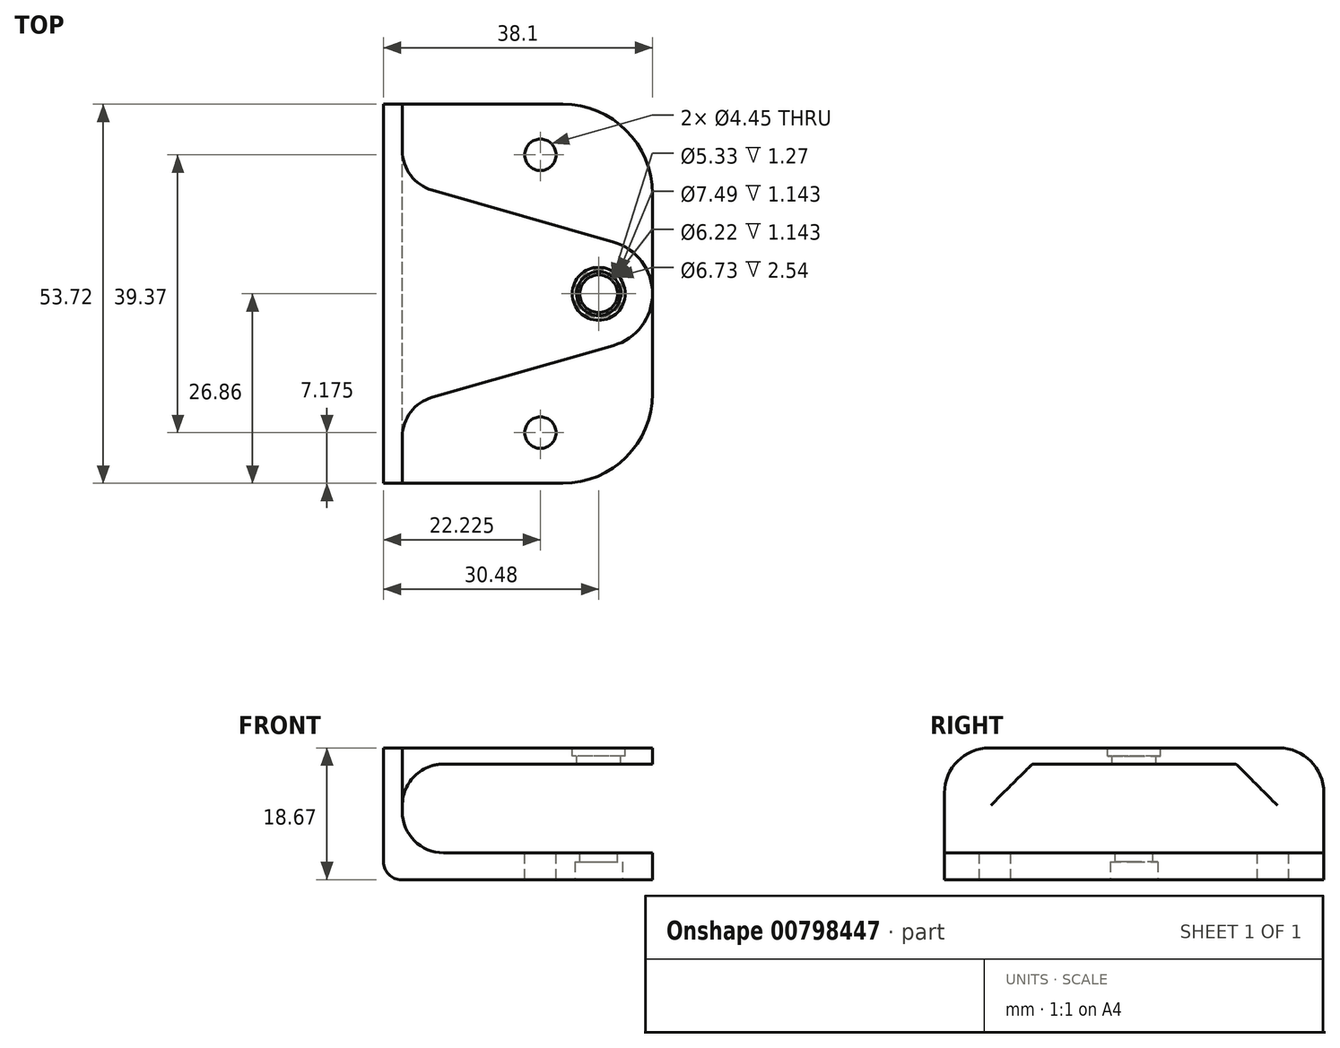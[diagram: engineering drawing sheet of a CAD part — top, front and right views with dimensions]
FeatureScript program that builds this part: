
annotation { "Feature Type Name" : "Feature", "Feature Type Description" : "" }
export const myFeature = defineFeature(function(context is Context, id is Id, definition is map)
    precondition{}
    {
        {
            var Q0;
            Q0=qCreatedBy(makeId("Front.planeOp"),FACE);
            var sketch = newSketch(context, id + "F0", { "sketchPlane" : qUnion([Q0])});
            skLineSegment(sketch, "E0", {"start": v(38.1, 0) * mm, "end": v(0, 0) * mm});
            skLineSegment(sketch, "E1", {"start": v(0, 0) * mm, "end": v(0, 18.67) * mm});
            skLineSegment(sketch, "E2", {"start": v(0, 18.67) * mm, "end": v(38.1, 18.67) * mm});
            skLineSegment(sketch, "E3", {"start": v(38.1, 18.67) * mm, "end": v(38.1, 16.38) * mm});
            skLineSegment(sketch, "E4", {"start": v(38.1, 16.38) * mm, "end": v(2.67, 16.38) * mm});
            skLineSegment(sketch, "E5", {"start": v(2.67, 16.38) * mm, "end": v(2.67, 3.8) * mm});
            skLineSegment(sketch, "E6", {"start": v(2.67, 3.8) * mm, "end": v(38.1, 3.81) * mm});
            skLineSegment(sketch, "E7", {"start": v(38.1, 3.81) * mm, "end": v(38.1, 0) * mm});
            skSolve(sketch);
        }
        {
            var Q0;
            Q0=makeQuery(id+"F0.imprint","IMPRINT",FACE,{"disambiguationData":[TD([[makeQuery(id+"F0.imprint","IMPRINT",EDGE,{"derivedFrom":sQuery(id+"F0.wireOp",EDGE,"E0")}),-1.0]])]});
            extrude(context, id + "F1", {"entities" : qUnion([Q0]), "endBound" : BoundingType.SYMMETRIC, "depth" : 53.72 * mm, "offsetDistance" : 25.4 * mm});
        }
        {
            var Q0;
            Q0=makeQuery(id+"F1.opExtrude","SWEPT_FACE",FACE,{"disambiguationData":[OSD([sQuery(id+"F0.wireOp",EDGE,"E6")])]});
            var sketch = newSketch(context, id + "F2", { "sketchPlane" : qUnion([Q0])});
            skCircle(sketch, "E8", {"center": v(22.23, 19.69) * mm, "radius": 2.22 * mm});
            skCircle(sketch, "E9", {"center": v(22.23, -19.69) * mm, "radius": 2.22 * mm});
            skCircle(sketch, "E10", {"center": v(30.48, 0) * mm, "radius": 2.67 * mm});
            skSolve(sketch);
        }
        {
            var Q0;
            Q0=makeQuery(id+"F2.imprint","IMPRINT",FACE,{"disambiguationData":[TD([[makeQuery(id+"F2.imprint","IMPRINT",EDGE,{"derivedFrom":sQuery(id+"F2.wireOp",EDGE,"E10")}),1.0]])]});
            var Q1;
            Q1=makeQuery(id+"F2.imprint","IMPRINT",FACE,{"disambiguationData":[TD([[makeQuery(id+"F2.imprint","IMPRINT",EDGE,{"derivedFrom":sQuery(id+"F2.wireOp",EDGE,"E8")}),1.0]])]});
            var Q2;
            Q2=makeQuery(id+"F2.imprint","IMPRINT",FACE,{"disambiguationData":[TD([[makeQuery(id+"F2.imprint","IMPRINT",EDGE,{"derivedFrom":sQuery(id+"F2.wireOp",EDGE,"E9")}),1.0]])]});
            extrude(context, id + "F3", {"entities" : qUnion([Q0, Q1, Q2]), "operationType" : NewBodyOperationType.REMOVE, "endBound" : BoundingType.THROUGH_ALL, "oppositeDirection" : true, "depth" : 25.4 * mm, "offsetDistance" : 25.4 * mm, "hasSecondDirection" : true, "secondDirectionBound" : SecondDirectionBoundingType.THROUGH_ALL, "secondDirectionOppositeDirection" : false, "secondDirectionDepth" : 25.4 * mm});
        }
        {
            var Q0;
            Q0=makeQuery(id+"F1.opExtrude","SWEPT_FACE",FACE,{"disambiguationData":[OSD([sQuery(id+"F0.wireOp",EDGE,"E2")])]});
            var sketch = newSketch(context, id + "F4", { "sketchPlane" : qUnion([Q0])});
            skLineSegment(sketch, "E11.0", {"start": v(2.67, -26.86) * mm, "end": v(2.67, 26.86) * mm, "construction": true});
            skCircle(sketch, "E12", {"center": v(30.48, 0) * mm, "radius": 7.62 * mm});
            skLineSegment(sketch, "E13", {"start": v(2.67, 15.87) * mm, "end": v(32.57, 7.33) * mm});
            skLineSegment(sketch, "E14", {"start": v(32.57, 7.33) * mm, "end": v(32.57, -7.33) * mm, "construction": true});
            skLineSegment(sketch, "E15", {"start": v(32.57, -7.33) * mm, "end": v(2.67, -15.88) * mm});
            skLineSegment(sketch, "E16", {"start": v(2.67, 15.87) * mm, "end": v(2.67, 26.86) * mm});
            skLineSegment(sketch, "E17", {"start": v(2.67, -15.88) * mm, "end": v(2.67, -26.86) * mm});
            skSolve(sketch);
        }
        {
            var Q0;
            {var subQ1=sQuery(id+"F4.wireOp",EDGE,"E13");Q0=makeQuery(id+"F4.imprint","IMPRINT",FACE,{"disambiguationData":[TD([[makeQuery(id+"F4.imprint","IMPRINT",EDGE,{"derivedFrom":subQ1}),1.0]])]});}
            var Q1;
            {var subQ2=sQuery(id+"F4.wireOp",EDGE,"E15");Q1=makeQuery(id+"F4.imprint","IMPRINT",FACE,{"disambiguationData":[TD([[makeQuery(id+"F4.imprint","IMPRINT",EDGE,{"derivedFrom":subQ2}),1.0]])]});}
            extrude(context, id + "F5", {"entities" : qUnion([Q0, Q1]), "operationType" : NewBodyOperationType.REMOVE, "endBound" : BoundingType.UP_TO_NEXT, "oppositeDirection" : true, "depth" : 25.4 * mm, "offsetDistance" : 25.4 * mm});
        }
        {
            var Q0;
            Q0=makeQuery(id+"F1.opExtrude","SWEPT_FACE",FACE,{"disambiguationData":[OSD([sQuery(id+"F0.wireOp",EDGE,"E2")])]});
            var sketch = newSketch(context, id + "F6", { "sketchPlane" : qUnion([Q0])});
            skCircle(sketch, "E18", {"center": v(30.48, 0) * mm, "radius": 3.75 * mm});
            skSolve(sketch);
        }
        {
            var Q0;
            Q0=makeQuery(id+"F6.imprint","IMPRINT",FACE,{"disambiguationData":[TD([[makeQuery(id+"F6.imprint","IMPRINT",EDGE,{"derivedFrom":sQuery(id+"F6.wireOp",EDGE,"E18")}),1.0]])]});
            extrude(context, id + "F7", {"entities" : qUnion([Q0]), "operationType" : NewBodyOperationType.REMOVE, "oppositeDirection" : true, "depth" : 1.14 * mm, "offsetDistance" : 25.4 * mm});
        }
        {
            var Q0;
            Q0=makeQuery(id+"F1.opExtrude","SWEPT_EDGE",EDGE,{"disambiguationData":[OSD([sQuery(id+"F0.wireOp",EDGE,"E5"),sQuery(id+"F0.wireOp",EDGE,"E6")])]});
            var Q1;
            Q1=makeQuery(id+"F1.opExtrude","SWEPT_EDGE",EDGE,{"disambiguationData":[OSD([sQuery(id+"F0.wireOp",EDGE,"E4"),sQuery(id+"F0.wireOp",EDGE,"E5")])]});
            var Q2;
            Q2=makeQuery(id+"F5.boolean.opBoolean","COPY",EDGE,{"derivedFrom":makeQuery(id+"F5.opExtrude","SWEPT_EDGE",EDGE,{"disambiguationData":[OSD([sQuery(id+"F4.wireOp",EDGE,"E13"),sQuery(id+"F4.wireOp",EDGE,"E16")])]})});
            var Q3;
            Q3=makeQuery(id+"F5.boolean.opBoolean","COPY",EDGE,{"derivedFrom":makeQuery(id+"F5.opExtrude","SWEPT_EDGE",EDGE,{"disambiguationData":[OSD([sQuery(id+"F4.wireOp",EDGE,"E15"),sQuery(id+"F4.wireOp",EDGE,"E17")])]})});
            fillet(context, id + "F8", {"entities" : qUnion([Q0, Q1, Q2, Q3]), "radius" : 5.84 * mm, "tangentPropagation" : true, "allowEdgeOverflow" : false});
        }
        {
            var Q0;
            Q0=makeQuery(id+"F1.opExtrude","CAP_EDGE",EDGE,{"disambiguationData":[OSD([sQuery(id+"F0.wireOp",EDGE,"E2")])],"isStart":true});
            var Q1;
            Q1=makeQuery(id+"F1.opExtrude","CAP_EDGE",EDGE,{"disambiguationData":[OSD([sQuery(id+"F0.wireOp",EDGE,"E2")])],"isStart":false});
            fillet(context, id + "F9", {"entities" : qUnion([Q0, Q1]), "radius" : 6.35 * mm, "tangentPropagation" : true, "allowEdgeOverflow" : false});
        }
        {
            var Q0;
            Q0=makeQuery(id+"F1.opExtrude","CAP_EDGE",EDGE,{"disambiguationData":[OSD([sQuery(id+"F0.wireOp",EDGE,"E7")])],"isStart":true});
            var Q1;
            Q1=makeQuery(id+"F1.opExtrude","CAP_EDGE",EDGE,{"disambiguationData":[OSD([sQuery(id+"F0.wireOp",EDGE,"E7")])],"isStart":false});
            fillet(context, id + "F10", {"entities" : qUnion([Q0, Q1]), "radius" : 12.7 * mm, "tangentPropagation" : true, "allowEdgeOverflow" : false});
        }
        {
            var Q0;
            Q0=makeQuery(id+"F1.opExtrude","SWEPT_EDGE",EDGE,{"disambiguationData":[OSD([sQuery(id+"F0.wireOp",EDGE,"E0"),sQuery(id+"F0.wireOp",EDGE,"E1")])]});
            fillet(context, id + "F11", {"entities" : qUnion([Q0]), "radius" : 2.54 * mm, "tangentPropagation" : true, "allowEdgeOverflow" : false});
        }
        {
            var Q0;
            Q0=makeQuery(id+"F7.boolean.opBoolean","COPY",FACE,{"derivedFrom":makeQuery(id+"F7.opExtrude","CAP_FACE",FACE,{"disambiguationData":[OSD([sQuery(id+"F0.wireOp",EDGE,"E2"),sQuery(id+"F2.wireOp",EDGE,"E10"),sQuery(id+"F6.wireOp",EDGE,"E18")])],"isStart":false})});
            var sketch = newSketch(context, id + "F12", { "sketchPlane" : qUnion([Q0])});
            skCircle(sketch, "E19", {"center": v(30.48, 0) * mm, "radius": 3.11 * mm});
            skSolve(sketch);
        }
        {
            var Q0;
            Q0=makeQuery(id+"F12.imprint","IMPRINT",FACE,{"disambiguationData":[TD([[makeQuery(id+"F12.imprint","IMPRINT",EDGE,{"derivedFrom":sQuery(id+"F12.wireOp",EDGE,"E19")}),1.0]])]});
            extrude(context, id + "F13", {"entities" : qUnion([Q0]), "operationType" : NewBodyOperationType.REMOVE, "endBound" : BoundingType.UP_TO_NEXT, "oppositeDirection" : true, "depth" : 25.4 * mm, "offsetDistance" : 25.4 * mm});
        }
        {
            var Q0;
            Q0=makeQuery(id+"F1.opExtrude","SWEPT_FACE",FACE,{"disambiguationData":[OSD([sQuery(id+"F0.wireOp",EDGE,"E0")])]});
            var sketch = newSketch(context, id + "F14", { "sketchPlane" : qUnion([Q0])});
            skCircle(sketch, "E20", {"center": v(30.48, 0) * mm, "radius": 3.37 * mm});
            skSolve(sketch);
        }
        {
            var Q0;
            Q0=makeQuery(id+"F14.imprint","IMPRINT",FACE,{"disambiguationData":[TD([[makeQuery(id+"F14.imprint","IMPRINT",EDGE,{"derivedFrom":sQuery(id+"F14.wireOp",EDGE,"E20")}),1.0]])]});
            extrude(context, id + "F15", {"entities" : qUnion([Q0]), "operationType" : NewBodyOperationType.REMOVE, "oppositeDirection" : true, "depth" : 2.54 * mm, "offsetDistance" : 25.4 * mm});
        }
    });
